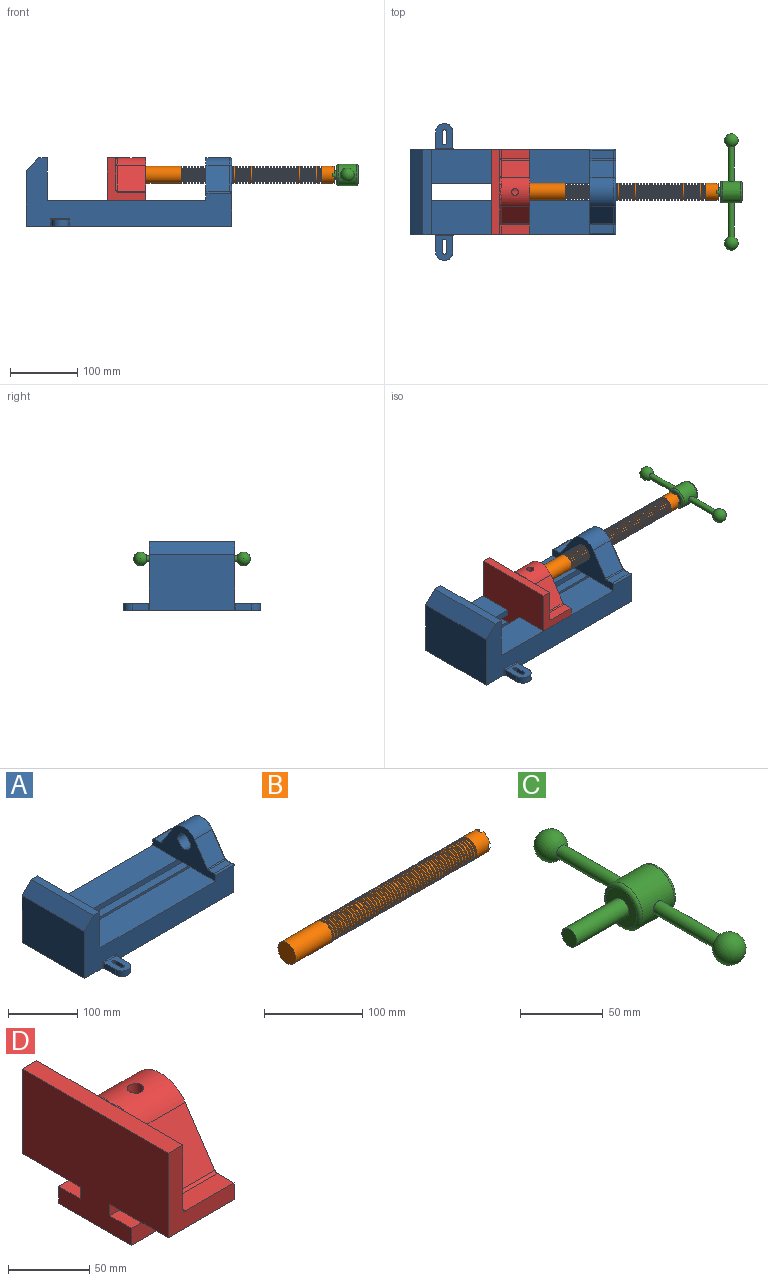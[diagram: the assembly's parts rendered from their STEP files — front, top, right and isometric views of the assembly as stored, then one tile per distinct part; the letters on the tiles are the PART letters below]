
ASSEMBLY  parts=4 mates=4
PART A: 61 faces, bbox 304.8x203.2x103.7 mm
  f0: plane 304.8x101.6mm, normal (0,1,0), area 13520.3mm2, adj f3,f4,f5,f6,f7,f8,f9,f16
  f1: plane 304.8x101.6mm, normal (0,-1,0), area 13520.3mm2, adj f2,f3,f5,f6,f7,f8,f9,f16
  f2: plane 234.95x50.8mm, normal (0,0,1), area 11935.5mm2, adj f1,f5,f16,f26
  f3: plane 127x99.06mm, normal (1,0,0), area 7097.5mm2, adj f0,f1,f9,f14,f17,f18,f19,f20
  f4: plane 234.95x50.8mm, normal (0,0,1), area 11935.5mm2, adj f0,f5,f16,f27
  f5: plane 127x101.6mm, normal (1,0,0), area 9516.1mm2, adj f0,f1,f2,f4,f6,f9,f18,f19
  f6: plane 127x12.7mm, normal (0,0,1), area 1612.9mm2, adj f0,f1,f5,f7
  f7: plane 127x19.05mm, normal (-0.71,0,0.71), area 3421.5mm2, adj f0,f1,f6,f8
  f8: plane 127x82.55mm, normal (-1,0,0), area 10483.8mm2, adj f0,f1,f7,f9
  f9: plane 304.8x203.2mm, normal (0,0,-1), area 33298.3mm2, adj f0,f1,f3,f5,f8,f21,f22,f39
  f10: plane 35.56x11.98mm, normal (0,0,1), area 426mm2, adj f16,f28,f29,f30
  f11: plane 38.43x35.56mm, normal (0,0.83,0.56), area 1645.4mm2, adj f12,f16,f29,f32
  f12: cylinder r=25.4mm len=42.19mm, axis (1,0,0), area 1770.2mm2, adj f11,f13,f16,f33
  f13: plane 38.43x35.56mm, normal (0,-0.83,0.56), area 1645.4mm2, adj f12,f16,f34,f35
  f14: cylinder r=12.7mm len=38.1mm, axis (1,0,0), area 3040.2mm2, adj f3,f16
  f15: plane 35.56x11.98mm, normal (0,0,1), area 426mm2, adj f16,f34,f36,f38
  f16: plane 127x63.5mm, normal (-1,0,0), area 4155.5mm2, adj f0,f1,f2,f4,f10,f11,f12,f13
  f17: plane 38.1x25.4mm, normal (0,0,-1), area 967.7mm2, adj f3,f16,f26,f27
  f18: plane 273.05x19.05mm, normal (0,0,-1), area 5201.6mm2, adj f3,f5,f19,f26
  f19: plane 273.05x12.7mm, normal (0,1,0), area 3467.7mm2, adj f3,f5,f18,f20
  f20: plane 273.05x19.05mm, normal (0,0,1), area 5201.6mm2, adj f3,f5,f19,f21
  f21: plane 273.05x16.51mm, normal (0,1,0), area 4508.1mm2, adj f3,f5,f9,f20
  f22: plane 273.05x16.51mm, normal (0,-1,0), area 4508.1mm2, adj f3,f5,f9,f23
  f23: plane 273.05x19.05mm, normal (0,0,1), area 5201.6mm2, adj f3,f5,f22,f24
  f24: plane 273.05x12.7mm, normal (0,-1,0), area 3467.7mm2, adj f3,f5,f23,f25
  f25: plane 273.05x19.05mm, normal (0,0,-1), area 5201.6mm2, adj f3,f5,f24,f27
  f26: plane 273.05x8.89mm, normal (0,1,0), area 2427.4mm2, adj f2,f3,f5,f17,f18
  f27: plane 273.05x8.89mm, normal (0,-1,0), area 2427.4mm2, adj f3,f4,f5,f17,f25
  f28: cylinder r=2.54mm len=38.1mm, axis (1,0,0), area 148.3mm2, adj f0,f10,f16,f30
  f29: cylinder r=2.54mm len=35.56mm, axis (-1,0,0), area 88.5mm2, adj f10,f11,f16,f31
  f30: cylinder r=2.54mm len=14.52mm, axis (0,1,0), area 54.3mm2, adj f3,f10,f28,f31
  f31: torus R=5.08mm, axis (-1,0,0), area 13.5mm2, adj f3,f29,f30,f32
  f32: cylinder r=2.54mm len=39.84mm, axis (0,0.56,-0.83), area 184.6mm2, adj f3,f11,f31,f33
  f33: torus R=22.86mm, axis (-1,0,0), area 191.4mm2, adj f3,f12,f32,f35
  f34: cylinder r=2.54mm len=35.56mm, axis (-1,0,0), area 88.5mm2, adj f13,f15,f16,f37
  f35: cylinder r=2.54mm len=39.84mm, axis (0,0.56,0.83), area 184.6mm2, adj f3,f13,f33,f37
  f36: cylinder r=2.54mm len=38.1mm, axis (-1,0,0), area 148.3mm2, adj f1,f15,f16,f38
  f37: torus R=5.08mm, axis (-1,0,0), area 13.5mm2, adj f3,f34,f35,f38
  f38: cylinder r=2.54mm len=14.52mm, axis (0,1,0), area 54.3mm2, adj f3,f15,f36,f37
  f39: plane 23.88x9.53mm, normal (-1,0,0), area 227.4mm2, adj f9,f45,f46,f60
  f40: plane 23.88x9.53mm, normal (1,0,0), area 227.4mm2, adj f9,f45,f46,f58
  f41: cylinder r=3.3mm len=9.53mm, axis (0,0,-1), area 98.8mm2, adj f9,f42,f44,f46
  f42: plane 15.62x9.53mm, normal (-1,0,0), area 148.8mm2, adj f9,f41,f43,f46
  f43: cylinder r=3.3mm len=9.53mm, axis (0,0,-1), area 98.8mm2, adj f9,f42,f44,f46
  f44: plane 15.62x9.53mm, normal (1,0,0), area 148.8mm2, adj f9,f41,f43,f46
  f45: cylinder r=12.7mm len=25.4mm, axis (0,0,-1), area 380mm2, adj f9,f39,f40,f46
  f46: plane 36.58x25.4mm, normal (0,0,1), area 722.4mm2, adj f39,f40,f41,f42,f43,f44,f45,f59
  f47: plane 23.88x9.53mm, normal (-1,0,0), area 227.4mm2, adj f9,f53,f54,f56
  f48: plane 23.88x9.53mm, normal (1,0,0), area 227.4mm2, adj f9,f53,f54,f55
  f49: cylinder r=3.3mm len=9.53mm, axis (0,0,-1), area 98.8mm2, adj f9,f50,f52,f54
  f50: plane 15.62x9.53mm, normal (-1,0,0), area 148.8mm2, adj f9,f49,f51,f54
  f51: cylinder r=3.3mm len=9.53mm, axis (0,0,-1), area 98.8mm2, adj f9,f50,f52,f54
  f52: plane 15.62x9.53mm, normal (1,0,0), area 148.8mm2, adj f9,f49,f51,f54
  f53: cylinder r=12.7mm len=25.4mm, axis (0,0,-1), area 380mm2, adj f9,f47,f48,f54
  f54: plane 36.58x25.4mm, normal (0,0,1), area 722.4mm2, adj f47,f48,f49,f50,f51,f52,f53,f57
  f55: cylinder r=1.52mm len=11.05mm, axis (0,0,-1), area 24.1mm2, adj f0,f9,f48,f57
  f56: cylinder r=1.52mm len=11.05mm, axis (0,0,1), area 24.1mm2, adj f0,f9,f47,f57
  f57: cylinder r=1.52mm len=28.45mm, axis (1,0,0), area 63.5mm2, adj f0,f54,f55,f56
  f58: cylinder r=1.52mm len=11.05mm, axis (0,0,1), area 24.1mm2, adj f1,f9,f40,f59
  f59: cylinder r=1.52mm len=28.45mm, axis (-1,0,0), area 63.5mm2, adj f1,f46,f58,f60
  f60: cylinder r=1.52mm len=11.05mm, axis (0,0,-1), area 24.1mm2, adj f1,f9,f39,f59
PART B: 220 faces, bbox 279.4x25.4x25.4 mm
  f0: cylinder r=12.7mm len=25.4mm, axis (-1,0,0), area 1468.2mm2, adj f1,f2,f3,f5,f7,f208,f209,f210
  f1: plane 9.9x9.9mm, normal (1,0,0), area 62.3mm2, adj f0,f4,f213,f216
  f2: plane 9.9x9.9mm, normal (1,0,0), area 62.3mm2, adj f0,f4,f210,f218
  f3: plane 9.9x9.9mm, normal (1,0,0), area 62.3mm2, adj f0,f4,f209,f212
  f4: cylinder r=6.35mm len=25.4mm, axis (1,0,0), area 960.3mm2, adj f1,f2,f3,f5,f6,f208,f209,f210
  f5: plane 9.9x9.9mm, normal (1,0,0), area 62.3mm2, adj f0,f4,f215,f217
  f6: plane 12.7x12.7mm, normal (1,0,0), area 126.7mm2, adj f4
  f7: cone r=12.7mm half-angle=76deg, axis (1,0,0), area 188mm2, adj f0,f9
  f8: cone r=10.16mm half-angle=76deg, axis (-1,0,0), area 188mm2, adj f9,f10
  f9: cylinder r=10.16mm len=20.32mm, axis (1,0,0), area 81.1mm2, adj f7,f8
  f10: cylinder r=12.7mm len=25.4mm, axis (-1,0,0), area 131.7mm2, adj f8,f11
  f11: cone r=12.7mm half-angle=76deg, axis (1,0,0), area 188mm2, adj f10,f13
  f12: cone r=10.16mm half-angle=76deg, axis (-1,0,0), area 188mm2, adj f13,f14
  f13: cylinder r=10.16mm len=20.32mm, axis (1,0,0), area 81.1mm2, adj f11,f12
  f14: cylinder r=12.7mm len=25.4mm, axis (-1,0,0), area 131.7mm2, adj f12,f15
  f15: cone r=12.7mm half-angle=76deg, axis (1,0,0), area 188mm2, adj f14,f17
  f16: cone r=10.16mm half-angle=76deg, axis (-1,0,0), area 188mm2, adj f17,f18
  f17: cylinder r=10.16mm len=20.32mm, axis (1,0,0), area 81.1mm2, adj f15,f16
  f18: cylinder r=12.7mm len=25.4mm, axis (-1,0,0), area 131.7mm2, adj f16,f19
  f19: cone r=12.7mm half-angle=76deg, axis (1,0,0), area 188mm2, adj f18,f21
  f20: cone r=10.16mm half-angle=76deg, axis (-1,0,0), area 188mm2, adj f21,f22
  f21: cylinder r=10.16mm len=20.32mm, axis (1,0,0), area 81.1mm2, adj f19,f20
  f22: cylinder r=12.7mm len=25.4mm, axis (-1,0,0), area 131.7mm2, adj f20,f23
  f23: cone r=12.7mm half-angle=76deg, axis (1,0,0), area 188mm2, adj f22,f25
  f24: cone r=10.16mm half-angle=76deg, axis (-1,0,0), area 188mm2, adj f25,f26
  f25: cylinder r=10.16mm len=20.32mm, axis (1,0,0), area 81.1mm2, adj f23,f24
  f26: cylinder r=12.7mm len=25.4mm, axis (-1,0,0), area 131.7mm2, adj f24,f27
  f27: cone r=12.7mm half-angle=76deg, axis (1,0,0), area 188mm2, adj f26,f29
  f28: cone r=10.16mm half-angle=76deg, axis (-1,0,0), area 188mm2, adj f29,f30
  f29: cylinder r=10.16mm len=20.32mm, axis (1,0,0), area 81.1mm2, adj f27,f28
  f30: cylinder r=12.7mm len=25.4mm, axis (-1,0,0), area 131.7mm2, adj f28,f31
  f31: cone r=12.7mm half-angle=76deg, axis (1,0,0), area 188mm2, adj f30,f33
  f32: cone r=10.16mm half-angle=76deg, axis (-1,0,0), area 188mm2, adj f33,f34
  f33: cylinder r=10.16mm len=20.32mm, axis (1,0,0), area 81.1mm2, adj f31,f32
  f34: cylinder r=12.7mm len=25.4mm, axis (-1,0,0), area 131.7mm2, adj f32,f35
  f35: cone r=12.7mm half-angle=76deg, axis (1,0,0), area 188mm2, adj f34,f37
  f36: cone r=10.16mm half-angle=76deg, axis (-1,0,0), area 188mm2, adj f37,f38
  f37: cylinder r=10.16mm len=20.32mm, axis (1,0,0), area 81.1mm2, adj f35,f36
  f38: cylinder r=12.7mm len=25.4mm, axis (-1,0,0), area 131.7mm2, adj f36,f39
  f39: cone r=12.7mm half-angle=76deg, axis (1,0,0), area 188mm2, adj f38,f41
  f40: cone r=10.16mm half-angle=76deg, axis (-1,0,0), area 188mm2, adj f41,f42
  f41: cylinder r=10.16mm len=20.32mm, axis (1,0,0), area 81.1mm2, adj f39,f40
  f42: cylinder r=12.7mm len=25.4mm, axis (-1,0,0), area 131.7mm2, adj f40,f43
  f43: cone r=12.7mm half-angle=76deg, axis (1,0,0), area 188mm2, adj f42,f45
  f44: cone r=10.16mm half-angle=76deg, axis (-1,0,0), area 188mm2, adj f45,f46
  f45: cylinder r=10.16mm len=20.32mm, axis (1,0,0), area 81.1mm2, adj f43,f44
  f46: cylinder r=12.7mm len=25.4mm, axis (-1,0,0), area 131.7mm2, adj f44,f47
  f47: cone r=12.7mm half-angle=76deg, axis (1,0,0), area 188mm2, adj f46,f49
  f48: cone r=10.16mm half-angle=76deg, axis (-1,0,0), area 188mm2, adj f49,f50
  f49: cylinder r=10.16mm len=20.32mm, axis (1,0,0), area 81.1mm2, adj f47,f48
  f50: cylinder r=12.7mm len=25.4mm, axis (-1,0,0), area 131.7mm2, adj f48,f51
  f51: cone r=12.7mm half-angle=76deg, axis (1,0,0), area 188mm2, adj f50,f53
  f52: cone r=10.16mm half-angle=76deg, axis (-1,0,0), area 188mm2, adj f53,f54
  f53: cylinder r=10.16mm len=20.32mm, axis (1,0,0), area 81.1mm2, adj f51,f52
  f54: cylinder r=12.7mm len=25.4mm, axis (-1,0,0), area 131.7mm2, adj f52,f55
  f55: cone r=12.7mm half-angle=76deg, axis (1,0,0), area 188mm2, adj f54,f57
  f56: cone r=10.16mm half-angle=76deg, axis (-1,0,0), area 188mm2, adj f57,f58
  f57: cylinder r=10.16mm len=20.32mm, axis (1,0,0), area 81.1mm2, adj f55,f56
  f58: cylinder r=12.7mm len=25.4mm, axis (-1,0,0), area 131.7mm2, adj f56,f59
  f59: cone r=12.7mm half-angle=76deg, axis (1,0,0), area 188mm2, adj f58,f61
  f60: cone r=10.16mm half-angle=76deg, axis (-1,0,0), area 188mm2, adj f61,f62
  f61: cylinder r=10.16mm len=20.32mm, axis (1,0,0), area 81.1mm2, adj f59,f60
  f62: cylinder r=12.7mm len=25.4mm, axis (-1,0,0), area 131.7mm2, adj f60,f63
  f63: cone r=12.7mm half-angle=76deg, axis (1,0,0), area 188mm2, adj f62,f65
  f64: cone r=10.16mm half-angle=76deg, axis (-1,0,0), area 188mm2, adj f65,f66
  f65: cylinder r=10.16mm len=20.32mm, axis (1,0,0), area 81.1mm2, adj f63,f64
  f66: cylinder r=12.7mm len=25.4mm, axis (-1,0,0), area 131.7mm2, adj f64,f67
  f67: cone r=12.7mm half-angle=76deg, axis (1,0,0), area 188mm2, adj f66,f69
  f68: cone r=10.16mm half-angle=76deg, axis (-1,0,0), area 188mm2, adj f69,f70
  f69: cylinder r=10.16mm len=20.32mm, axis (1,0,0), area 81.1mm2, adj f67,f68
  f70: cylinder r=12.7mm len=25.4mm, axis (-1,0,0), area 131.7mm2, adj f68,f71
  f71: cone r=12.7mm half-angle=76deg, axis (1,0,0), area 188mm2, adj f70,f73
  f72: cone r=10.16mm half-angle=76deg, axis (-1,0,0), area 188mm2, adj f73,f74
  f73: cylinder r=10.16mm len=20.32mm, axis (1,0,0), area 81.1mm2, adj f71,f72
  f74: cylinder r=12.7mm len=25.4mm, axis (-1,0,0), area 131.7mm2, adj f72,f75
  f75: cone r=12.7mm half-angle=76deg, axis (1,0,0), area 188mm2, adj f74,f77
  f76: cone r=10.16mm half-angle=76deg, axis (-1,0,0), area 188mm2, adj f77,f78
  f77: cylinder r=10.16mm len=20.32mm, axis (1,0,0), area 81.1mm2, adj f75,f76
  f78: cylinder r=12.7mm len=25.4mm, axis (-1,0,0), area 131.7mm2, adj f76,f79
  f79: cone r=12.7mm half-angle=76deg, axis (1,0,0), area 188mm2, adj f78,f81
  f80: cone r=10.16mm half-angle=76deg, axis (-1,0,0), area 188mm2, adj f81,f82
  f81: cylinder r=10.16mm len=20.32mm, axis (1,0,0), area 81.1mm2, adj f79,f80
  f82: cylinder r=12.7mm len=25.4mm, axis (-1,0,0), area 131.7mm2, adj f80,f83
  f83: cone r=12.7mm half-angle=76deg, axis (1,0,0), area 188mm2, adj f82,f85
  f84: cone r=10.16mm half-angle=76deg, axis (-1,0,0), area 188mm2, adj f85,f86
  f85: cylinder r=10.16mm len=20.32mm, axis (1,0,0), area 81.1mm2, adj f83,f84
  f86: cylinder r=12.7mm len=25.4mm, axis (-1,0,0), area 131.7mm2, adj f84,f87
  f87: cone r=12.7mm half-angle=76deg, axis (1,0,0), area 188mm2, adj f86,f89
  f88: cone r=10.16mm half-angle=76deg, axis (-1,0,0), area 188mm2, adj f89,f90
  f89: cylinder r=10.16mm len=20.32mm, axis (1,0,0), area 81.1mm2, adj f87,f88
  f90: cylinder r=12.7mm len=25.4mm, axis (-1,0,0), area 131.7mm2, adj f88,f91
  f91: cone r=12.7mm half-angle=76deg, axis (1,0,0), area 188mm2, adj f90,f93
  f92: cone r=10.16mm half-angle=76deg, axis (-1,0,0), area 188mm2, adj f93,f94
  f93: cylinder r=10.16mm len=20.32mm, axis (1,0,0), area 81.1mm2, adj f91,f92
  f94: cylinder r=12.7mm len=25.4mm, axis (-1,0,0), area 131.7mm2, adj f92,f95
  f95: cone r=12.7mm half-angle=76deg, axis (1,0,0), area 188mm2, adj f94,f97
  f96: cone r=10.16mm half-angle=76deg, axis (-1,0,0), area 188mm2, adj f97,f98
  f97: cylinder r=10.16mm len=20.32mm, axis (1,0,0), area 81.1mm2, adj f95,f96
  f98: cylinder r=12.7mm len=25.4mm, axis (-1,0,0), area 131.7mm2, adj f96,f99
  f99: cone r=12.7mm half-angle=76deg, axis (1,0,0), area 188mm2, adj f98,f101
  f100: cone r=10.16mm half-angle=76deg, axis (-1,0,0), area 188mm2, adj f101,f102
  f101: cylinder r=10.16mm len=20.32mm, axis (1,0,0), area 81.1mm2, adj f99,f100
  f102: cylinder r=12.7mm len=25.4mm, axis (-1,0,0), area 131.7mm2, adj f100,f103
  f103: cone r=12.7mm half-angle=76deg, axis (1,0,0), area 188mm2, adj f102,f105
  f104: cone r=10.16mm half-angle=76deg, axis (-1,0,0), area 188mm2, adj f105,f106
  f105: cylinder r=10.16mm len=20.32mm, axis (1,0,0), area 81.1mm2, adj f103,f104
  f106: cylinder r=12.7mm len=25.4mm, axis (-1,0,0), area 131.7mm2, adj f104,f107
  f107: cone r=12.7mm half-angle=76deg, axis (1,0,0), area 188mm2, adj f106,f109
  f108: cone r=10.16mm half-angle=76deg, axis (-1,0,0), area 188mm2, adj f109,f110
  f109: cylinder r=10.16mm len=20.32mm, axis (1,0,0), area 81.1mm2, adj f107,f108
  f110: cylinder r=12.7mm len=25.4mm, axis (-1,0,0), area 131.7mm2, adj f108,f111
  f111: cone r=12.7mm half-angle=76deg, axis (1,0,0), area 188mm2, adj f110,f113
  f112: cone r=10.16mm half-angle=76deg, axis (-1,0,0), area 188mm2, adj f113,f114
  f113: cylinder r=10.16mm len=20.32mm, axis (1,0,0), area 81.1mm2, adj f111,f112
  f114: cylinder r=12.7mm len=25.4mm, axis (-1,0,0), area 131.7mm2, adj f112,f115
  f115: cone r=12.7mm half-angle=76deg, axis (1,0,0), area 188mm2, adj f114,f117
  f116: cone r=10.16mm half-angle=76deg, axis (-1,0,0), area 188mm2, adj f117,f118
  f117: cylinder r=10.16mm len=20.32mm, axis (1,0,0), area 81.1mm2, adj f115,f116
  f118: cylinder r=12.7mm len=25.4mm, axis (-1,0,0), area 131.7mm2, adj f116,f119
  f119: cone r=12.7mm half-angle=76deg, axis (1,0,0), area 188mm2, adj f118,f121
  f120: cone r=10.16mm half-angle=76deg, axis (-1,0,0), area 188mm2, adj f121,f122
  f121: cylinder r=10.16mm len=20.32mm, axis (1,0,0), area 81.1mm2, adj f119,f120
  f122: cylinder r=12.7mm len=25.4mm, axis (-1,0,0), area 131.7mm2, adj f120,f123
  f123: cone r=12.7mm half-angle=76deg, axis (1,0,0), area 188mm2, adj f122,f125
  f124: cone r=10.16mm half-angle=76deg, axis (-1,0,0), area 188mm2, adj f125,f126
  f125: cylinder r=10.16mm len=20.32mm, axis (1,0,0), area 81.1mm2, adj f123,f124
  f126: cylinder r=12.7mm len=25.4mm, axis (-1,0,0), area 131.7mm2, adj f124,f127
  f127: cone r=12.7mm half-angle=76deg, axis (1,0,0), area 188mm2, adj f126,f129
  f128: cone r=10.16mm half-angle=76deg, axis (-1,0,0), area 188mm2, adj f129,f130
  f129: cylinder r=10.16mm len=20.32mm, axis (1,0,0), area 81.1mm2, adj f127,f128
  f130: cylinder r=12.7mm len=25.4mm, axis (-1,0,0), area 131.7mm2, adj f128,f131
  f131: cone r=12.7mm half-angle=76deg, axis (1,0,0), area 188mm2, adj f130,f133
  f132: cone r=10.16mm half-angle=76deg, axis (-1,0,0), area 188mm2, adj f133,f134
  f133: cylinder r=10.16mm len=20.32mm, axis (1,0,0), area 81.1mm2, adj f131,f132
  f134: cylinder r=12.7mm len=25.4mm, axis (-1,0,0), area 131.7mm2, adj f132,f135
  f135: cone r=12.7mm half-angle=76deg, axis (1,0,0), area 188mm2, adj f134,f137
  f136: cone r=10.16mm half-angle=76deg, axis (-1,0,0), area 188mm2, adj f137,f138
  f137: cylinder r=10.16mm len=20.32mm, axis (1,0,0), area 81.1mm2, adj f135,f136
  f138: cylinder r=12.7mm len=25.4mm, axis (-1,0,0), area 131.7mm2, adj f136,f139
  f139: cone r=12.7mm half-angle=76deg, axis (1,0,0), area 188mm2, adj f138,f141
  f140: cone r=10.16mm half-angle=76deg, axis (-1,0,0), area 188mm2, adj f141,f142
  f141: cylinder r=10.16mm len=20.32mm, axis (1,0,0), area 81.1mm2, adj f139,f140
  f142: cylinder r=12.7mm len=25.4mm, axis (-1,0,0), area 131.7mm2, adj f140,f143
  f143: cone r=12.7mm half-angle=76deg, axis (1,0,0), area 188mm2, adj f142,f145
  f144: cone r=10.16mm half-angle=76deg, axis (-1,0,0), area 188mm2, adj f145,f146
  f145: cylinder r=10.16mm len=20.32mm, axis (1,0,0), area 81.1mm2, adj f143,f144
  f146: cylinder r=12.7mm len=25.4mm, axis (-1,0,0), area 131.7mm2, adj f144,f147
  f147: cone r=12.7mm half-angle=76deg, axis (1,0,0), area 188mm2, adj f146,f149
  f148: cone r=10.16mm half-angle=76deg, axis (-1,0,0), area 188mm2, adj f149,f150
  f149: cylinder r=10.16mm len=20.32mm, axis (1,0,0), area 81.1mm2, adj f147,f148
  f150: cylinder r=12.7mm len=25.4mm, axis (-1,0,0), area 131.7mm2, adj f148,f151
  f151: cone r=12.7mm half-angle=76deg, axis (1,0,0), area 188mm2, adj f150,f153
  f152: cone r=10.16mm half-angle=76deg, axis (-1,0,0), area 188mm2, adj f153,f154
  f153: cylinder r=10.16mm len=20.32mm, axis (1,0,0), area 81.1mm2, adj f151,f152
  f154: cylinder r=12.7mm len=25.4mm, axis (-1,0,0), area 131.7mm2, adj f152,f155
  f155: cone r=12.7mm half-angle=76deg, axis (1,0,0), area 188mm2, adj f154,f157
  f156: cone r=10.16mm half-angle=76deg, axis (-1,0,0), area 188mm2, adj f157,f158
  f157: cylinder r=10.16mm len=20.32mm, axis (1,0,0), area 81.1mm2, adj f155,f156
  f158: cylinder r=12.7mm len=25.4mm, axis (-1,0,0), area 131.7mm2, adj f156,f159
  f159: cone r=12.7mm half-angle=76deg, axis (1,0,0), area 188mm2, adj f158,f161
  f160: cone r=10.16mm half-angle=76deg, axis (-1,0,0), area 188mm2, adj f161,f162
  f161: cylinder r=10.16mm len=20.32mm, axis (1,0,0), area 81.1mm2, adj f159,f160
  f162: cylinder r=12.7mm len=25.4mm, axis (-1,0,0), area 131.7mm2, adj f160,f163
  f163: cone r=12.7mm half-angle=76deg, axis (1,0,0), area 188mm2, adj f162,f165
  f164: cone r=10.16mm half-angle=76deg, axis (-1,0,0), area 188mm2, adj f165,f166
  f165: cylinder r=10.16mm len=20.32mm, axis (1,0,0), area 81.1mm2, adj f163,f164
  f166: cylinder r=12.7mm len=25.4mm, axis (-1,0,0), area 131.7mm2, adj f164,f167
  f167: cone r=12.7mm half-angle=76deg, axis (1,0,0), area 188mm2, adj f166,f169
  f168: cone r=10.16mm half-angle=76deg, axis (-1,0,0), area 188mm2, adj f169,f170
  f169: cylinder r=10.16mm len=20.32mm, axis (1,0,0), area 81.1mm2, adj f167,f168
  f170: cylinder r=12.7mm len=25.4mm, axis (-1,0,0), area 131.7mm2, adj f168,f171
  f171: cone r=12.7mm half-angle=76deg, axis (1,0,0), area 188mm2, adj f170,f173
  f172: cone r=10.16mm half-angle=76deg, axis (-1,0,0), area 188mm2, adj f173,f174
  f173: cylinder r=10.16mm len=20.32mm, axis (1,0,0), area 81.1mm2, adj f171,f172
  f174: cylinder r=12.7mm len=25.4mm, axis (-1,0,0), area 131.7mm2, adj f172,f175
  f175: cone r=12.7mm half-angle=76deg, axis (1,0,0), area 188mm2, adj f174,f177
  f176: cone r=10.16mm half-angle=76deg, axis (-1,0,0), area 188mm2, adj f177,f178
  f177: cylinder r=10.16mm len=20.32mm, axis (1,0,0), area 81.1mm2, adj f175,f176
  f178: cylinder r=12.7mm len=25.4mm, axis (-1,0,0), area 131.7mm2, adj f176,f179
  f179: cone r=12.7mm half-angle=76deg, axis (1,0,0), area 188mm2, adj f178,f181
  f180: cone r=10.16mm half-angle=76deg, axis (-1,0,0), area 188mm2, adj f181,f182
  f181: cylinder r=10.16mm len=20.32mm, axis (1,0,0), area 81.1mm2, adj f179,f180
  f182: cylinder r=12.7mm len=25.4mm, axis (-1,0,0), area 131.7mm2, adj f180,f183
  f183: cone r=12.7mm half-angle=76deg, axis (1,0,0), area 188mm2, adj f182,f185
  f184: cone r=10.16mm half-angle=76deg, axis (-1,0,0), area 188mm2, adj f185,f186
  f185: cylinder r=10.16mm len=20.32mm, axis (1,0,0), area 81.1mm2, adj f183,f184
  f186: cylinder r=12.7mm len=25.4mm, axis (-1,0,0), area 131.7mm2, adj f184,f187
  f187: cone r=12.7mm half-angle=76deg, axis (1,0,0), area 188mm2, adj f186,f189
  f188: cone r=10.16mm half-angle=76deg, axis (-1,0,0), area 188mm2, adj f189,f190
  f189: cylinder r=10.16mm len=20.32mm, axis (1,0,0), area 81.1mm2, adj f187,f188
  f190: cylinder r=12.7mm len=25.4mm, axis (-1,0,0), area 131.7mm2, adj f188,f191
  f191: cone r=12.7mm half-angle=76deg, axis (1,0,0), area 188mm2, adj f190,f193
  f192: cone r=10.16mm half-angle=76deg, axis (-1,0,0), area 188mm2, adj f193,f194
  f193: cylinder r=10.16mm len=20.32mm, axis (1,0,0), area 81.1mm2, adj f191,f192
  f194: cylinder r=12.7mm len=25.4mm, axis (-1,0,0), area 131.7mm2, adj f192,f195
  f195: cone r=12.7mm half-angle=76deg, axis (1,0,0), area 188mm2, adj f194,f197
  f196: cone r=10.16mm half-angle=76deg, axis (-1,0,0), area 188mm2, adj f197,f198
  f197: cylinder r=10.16mm len=20.32mm, axis (1,0,0), area 81.1mm2, adj f195,f196
  f198: cylinder r=12.7mm len=25.4mm, axis (-1,0,0), area 131.7mm2, adj f196,f199
  f199: cone r=12.7mm half-angle=76deg, axis (1,0,0), area 188mm2, adj f198,f201
  f200: cone r=10.16mm half-angle=76deg, axis (-1,0,0), area 188mm2, adj f201,f202
  f201: cylinder r=10.16mm len=20.32mm, axis (1,0,0), area 81.1mm2, adj f199,f200
  f202: cylinder r=12.7mm len=25.4mm, axis (-1,0,0), area 131.7mm2, adj f200,f203
  f203: cone r=12.7mm half-angle=76deg, axis (1,0,0), area 188mm2, adj f202,f205
  f204: cone r=10.16mm half-angle=76deg, axis (-1,0,0), area 188mm2, adj f205,f207
  f205: cylinder r=10.16mm len=20.32mm, axis (1,0,0), area 81.1mm2, adj f203,f204
  f206: plane 25.4x25.4mm, normal (-1,0,0), area 506.7mm2, adj f207
  f207: cylinder r=12.7mm len=52.45mm, axis (-1,0,0), area 4185.4mm2, adj f204,f206
  f208: plane 6.88x5.08mm, normal (1,0,0), area 32.7mm2, adj f0,f4,f209,f210
  f209: plane 6.62x2.54mm, normal (0,-1,0), area 16.8mm2, adj f0,f3,f4,f208
  f210: plane 6.62x2.54mm, normal (0,1,0), area 16.8mm2, adj f0,f2,f4,f208
  f211: plane 6.88x5.08mm, normal (1,0,0), area 32.7mm2, adj f0,f4,f212,f213
  f212: plane 6.62x2.54mm, normal (0,0,1), area 16.8mm2, adj f0,f3,f4,f211
  f213: plane 6.62x2.54mm, normal (0,0,-1), area 16.8mm2, adj f0,f1,f4,f211
  f214: plane 6.88x5.08mm, normal (1,0,0), area 32.7mm2, adj f0,f4,f215,f216
  f215: plane 6.62x2.54mm, normal (0,1,0), area 16.8mm2, adj f0,f4,f5,f214
  f216: plane 6.62x2.54mm, normal (0,-1,0), area 16.8mm2, adj f0,f1,f4,f214
  f217: plane 6.62x2.54mm, normal (0,0,-1), area 16.8mm2, adj f0,f4,f5,f219
  f218: plane 6.62x2.54mm, normal (0,0,1), area 16.8mm2, adj f0,f2,f4,f219
  f219: plane 6.88x5.08mm, normal (1,0,0), area 32.7mm2, adj f0,f4,f217,f218
PART C: 11 faces, bbox 76.2x172.7x34.4 mm
  f0: sphere r=10.16mm, area 1231.8mm2, adj f1
  f1: cylinder r=4.45mm len=51.82mm, axis (0,1,0), area 1438.5mm2, adj f0,f4
  f2: sphere r=10.16mm, area 1231.8mm2, adj f3
  f3: cylinder r=4.45mm len=51.82mm, axis (0,1,0), area 1438.5mm2, adj f2,f4
  f4: cylinder r=15.88mm len=31.75mm, axis (-1,0,0), area 2534.7mm2, adj f1,f3,f9,f10
  f5: cylinder r=6.35mm len=44.45mm, axis (-1,0,0), area 1773.5mm2, adj f6,f8
  f6: plane 12.7x12.7mm, normal (-1,0,0), area 126.7mm2, adj f5
  f7: plane 26.67x26.67mm, normal (1,0,0), area 558.6mm2, adj f10
  f8: plane 26.67x26.67mm, normal (-1,0,0), area 432mm2, adj f5,f9
  f9: torus R=13.33mm, axis (1,0,0), area 374.8mm2, adj f4,f8
  f10: torus R=13.33mm, axis (1,0,0), area 374.8mm2, adj f4,f7
PART D: 36 faces, bbox 57.2x127x89 mm
  f0: plane 57.15x50.8mm, normal (0,0,-1), area 2903.2mm2, adj f6,f9,f10,f23
  f1: cylinder r=12.7mm len=44.45mm, axis (1,0,0), area 3464.3mm2, adj f6,f15,f16
  f2: plane 41.91x14.52mm, normal (0,0,1), area 608.5mm2, adj f6,f11,f24,f25
  f3: plane 51.86x48.26mm, normal (1,0,0), area 1495.7mm2, adj f8,f10,f31,f33,f35
  f4: plane 51.86x48.26mm, normal (1,0,0), area 1495.7mm2, adj f8,f11,f24,f28,f29
  f5: plane 57.15x50.8mm, normal (0,0,-1), area 2903.2mm2, adj f6,f9,f11,f22
  f6: plane 127x85.09mm, normal (1,0,0), area 5190.6mm2, adj f0,f1,f2,f5,f7,f10,f11,f12
  f7: plane 41.91x14.52mm, normal (0,0,1), area 608.5mm2, adj f6,f10,f30,f31
  f8: plane 127x12.7mm, normal (0,0,1), area 1612.9mm2, adj f3,f4,f9,f10,f11,f26,f34
  f9: plane 127x85.09mm, normal (-1,0,0), area 9096.8mm2, adj f0,f5,f8,f10,f11,f17,f18,f19
  f10: plane 63.5x57.15mm, normal (0,-1,0), area 1372.3mm2, adj f0,f3,f6,f7,f8,f9,f31
  f11: plane 63.5x57.15mm, normal (0,1,0), area 1372.3mm2, adj f2,f4,f5,f6,f8,f9,f24
  f12: plane 41.91x38.43mm, normal (0,-0.83,0.56), area 1939.2mm2, adj f6,f13,f30,f33
  f13: cylinder r=25.4mm len=44.45mm, axis (1,0,0), area 2026.5mm2, adj f6,f12,f14,f16,f26,f28,f34,f35
  f14: plane 41.91x38.43mm, normal (0,0.83,0.56), area 1939.2mm2, adj f6,f13,f25,f29
  f15: plane 25.4x25.4mm, normal (1,0,0), area 506.7mm2, adj f1
  f16: cylinder r=5.08mm len=13.76mm, axis (0,0,1), area 414mm2, adj f1,f13
  f17: plane 57.15x19.05mm, normal (0,0,1), area 1088.7mm2, adj f6,f9,f18,f23
  f18: plane 57.15x12.7mm, normal (0,-1,0), area 725.8mm2, adj f6,f9,f17,f19
  f19: plane 63.5x57.15mm, normal (0,0,-1), area 3629mm2, adj f6,f9,f18,f20
  f20: plane 57.15x12.7mm, normal (0,1,0), area 725.8mm2, adj f6,f9,f19,f21
  f21: plane 57.15x19.05mm, normal (0,0,1), area 1088.7mm2, adj f6,f9,f20,f22
  f22: plane 57.15x8.89mm, normal (0,1,0), area 508.1mm2, adj f5,f6,f9,f21
  f23: plane 57.15x8.89mm, normal (0,-1,0), area 508.1mm2, adj f0,f6,f9,f17
  f24: cylinder r=2.54mm len=14.52mm, axis (0,-1,0), area 57.9mm2, adj f2,f4,f11,f27
  f25: cylinder r=2.54mm len=41.91mm, axis (1,0,0), area 104.3mm2, adj f2,f6,f14,f27
  f26: bspline ~12.24x2.8mm, area 20.9mm2, adj f8,f13,f28
  f27: sphere r=2.54mm, area 6.3mm2, adj f24,f25,f29
  f28: torus R=27.94mm, axis (1,0,0), area 57.8mm2, adj f4,f13,f26,f29
  f29: cylinder r=2.54mm len=39.84mm, axis (0,-0.56,0.83), area 184.6mm2, adj f4,f14,f27,f28
  f30: cylinder r=2.54mm len=41.91mm, axis (1,0,0), area 104.3mm2, adj f6,f7,f12,f32
  f31: cylinder r=2.54mm len=14.52mm, axis (0,-1,0), area 57.9mm2, adj f3,f7,f10,f32
  f32: sphere r=2.54mm, area 6.3mm2, adj f30,f31,f33
  f33: cylinder r=2.54mm len=39.84mm, axis (0,-0.56,-0.83), area 184.6mm2, adj f3,f12,f32,f35
  f34: bspline ~12.24x2.8mm, area 20.9mm2, adj f8,f13,f35
  f35: torus R=27.94mm, axis (1,0,0), area 57.8mm2, adj f3,f13,f33,f34
PLACE A t=(116.25,-0.53,-50.48)mm fixed
PLACE B rot(axis=(0.02,1,-0.07),0deg) t=(249.6,-0.53,-50.48)mm
PLACE C t=(233.72,-0.53,-50.48)mm
PLACE D t=(205.15,-0.53,-50.48)mm
MATE slider D.f0 <-> A.f2  axis (0,0,-1) through (-39.33,-38.63,-12.38)mm
MATE cylindrical B.f7 <-> A.f12  axis (1,0,0) through (68.75,-0.53,25.72)mm
MATE fastened C.f5 <-> B.f4  axis (-1,0,0) through (249.6,-0.53,25.72)mm
MATE fastened B.f7 <-> D.f28  axis (-1,0,0) through (-10.75,-0.53,25.72)mm
